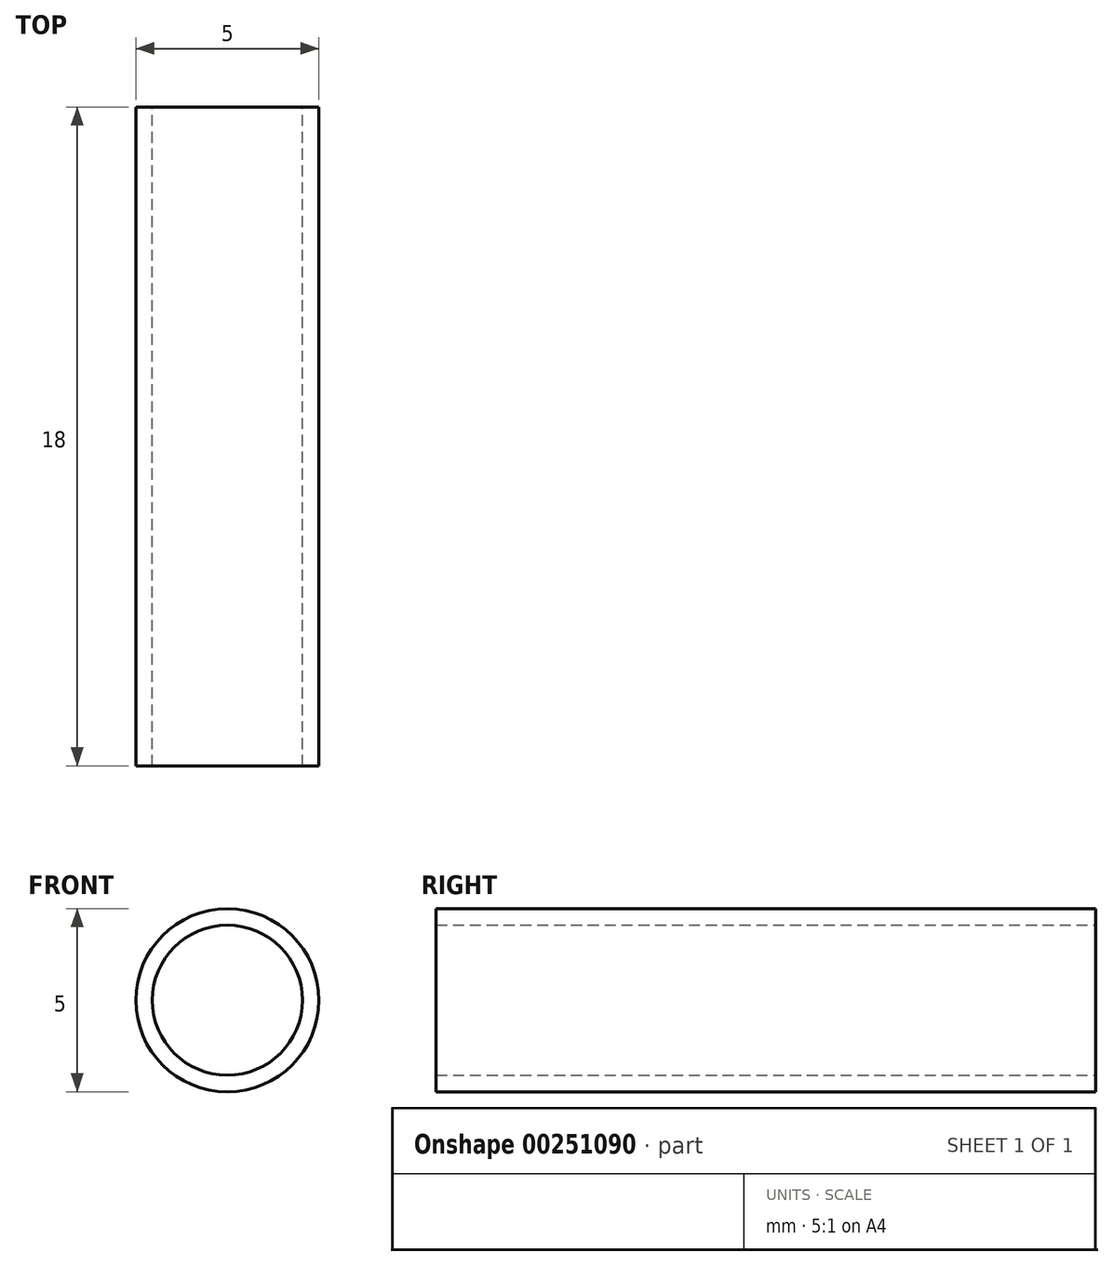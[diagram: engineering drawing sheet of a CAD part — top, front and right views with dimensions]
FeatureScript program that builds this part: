
annotation { "Feature Type Name" : "Feature", "Feature Type Description" : "" }
export const myFeature = defineFeature(function(context is Context, id is Id, definition is map)
    precondition{}
    {
        {
            var Q0;
            Q0=qCreatedBy(makeId("Front.planeOp"),FACE);
            var sketch = newSketch(context, id + "F0", { "sketchPlane" : qUnion([Q0])});
            skCircle(sketch, "E0", {"center": v(0, 0) * mm, "radius": 2.5 * mm});
            skCircle(sketch, "E1.0", {"center": v(0, 0) * mm, "radius": 2.05 * mm});
            skSolve(sketch);
        }
        {
            var Q0;
            Q0=makeQuery(id+"F0.imprint","IMPRINT",FACE,{"disambiguationData":[TD([[makeQuery(id+"F0.imprint","IMPRINT",EDGE,{"derivedFrom":sQuery(id+"F0.wireOp",EDGE,"E0")}),1.0]])]});
            extrude(context, id + "F1", {"entities" : qUnion([Q0]), "depth" : 18 * mm});
        }
    });
